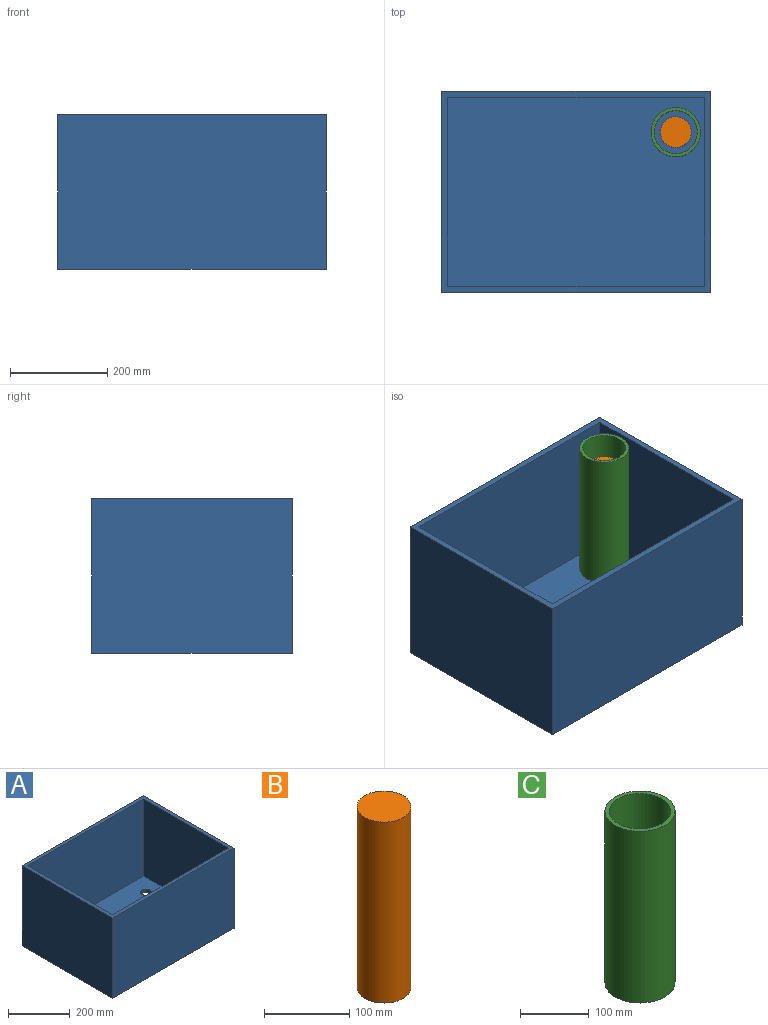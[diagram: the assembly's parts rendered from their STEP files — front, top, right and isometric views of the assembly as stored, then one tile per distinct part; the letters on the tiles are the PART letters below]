
ASSEMBLY  parts=3 mates=4
PART A: 12 faces, bbox 553.7x414x317.5 mm
  f0: plane 553.72x414.02mm, normal (0,0,1), area 23935.4mm2, adj f1,f2,f3,f4,f6,f7,f8,f9
  f1: plane 414.02x317.5mm, normal (-1,0,0), area 131451.3mm2, adj f0,f2,f4,f5
  f2: plane 553.72x317.5mm, normal (0,-1,0), area 175806.1mm2, adj f0,f1,f3,f5
  f3: plane 414.02x317.5mm, normal (1,0,0), area 131451.3mm2, adj f0,f2,f4,f5
  f4: plane 553.72x317.5mm, normal (0,1,0), area 175806.1mm2, adj f0,f1,f3,f5
  f5: plane 553.72x414.02mm, normal (0,0,-1), area 228293.2mm2, adj f1,f2,f3,f4,f11
  f6: plane 388.62x304.8mm, normal (1,0,0), area 118451.4mm2, adj f0,f7,f9,f10
  f7: plane 528.32x304.8mm, normal (0,1,0), area 161031.9mm2, adj f0,f6,f8,f10
  f8: plane 388.62x304.8mm, normal (-1,0,0), area 118451.4mm2, adj f0,f7,f9,f10
  f9: plane 528.32x304.8mm, normal (0,-1,0), area 161031.9mm2, adj f0,f6,f8,f10
  f10: plane 528.32x388.62mm, normal (0,0,1), area 204357.7mm2, adj f6,f7,f8,f9,f11
  f11: cylinder r=17.46mm len=34.93mm, axis (0,0,1), area 1393.4mm2, adj f5,f10
PART B: 5 faces, bbox 63.5x63.5x260.4 mm
  f0: cylinder r=25.4mm len=254mm, axis (0,0,-1), area 40536.6mm2, adj f2,f3
  f1: cylinder r=31.75mm len=260.35mm, axis (0,0,-1), area 51937.5mm2, adj f2,f4
  f2: plane 63.5x63.5mm, normal (0,0,-1), area 1140.1mm2, adj f0,f1
  f3: plane 50.8x50.8mm, normal (0,0,-1), area 2026.8mm2, adj f0
  f4: plane 63.5x63.5mm, normal (0,0,1), area 3166.9mm2, adj f1
PART C: 4 faces, bbox 101.6x101.6x304.8 mm
  f0: cylinder r=44.45mm len=304.8mm, axis (0,0,-1), area 85126.9mm2, adj f2,f3
  f1: cylinder r=50.8mm len=304.8mm, axis (0,0,-1), area 97287.8mm2, adj f2,f3
  f2: plane 101.6x101.6mm, normal (0,0,1), area 1900.2mm2, adj f0,f1
  f3: plane 101.6x101.6mm, normal (0,0,-1), area 1900.2mm2, adj f0,f1
PLACE A at identity
PLACE B t=(482.6,330.2,12.7)mm
PLACE C t=(482.6,330.2,12.7)mm
MATE cylindrical B.f1 <-> A.f11  axis (0,0,-1) through (482.6,330.2,142.88)mm
MATE planar A.f10 <-> C.f1  axis (0,0,1) through (275.9,206.43,12.7)mm
MATE planar B.f1 <-> A.f10  axis (0,0,-1) through (482.6,330.2,12.7)mm
MATE cylindrical C.f1 <-> B.f1  axis (0,0,-1) through (482.6,330.2,165.1)mm
